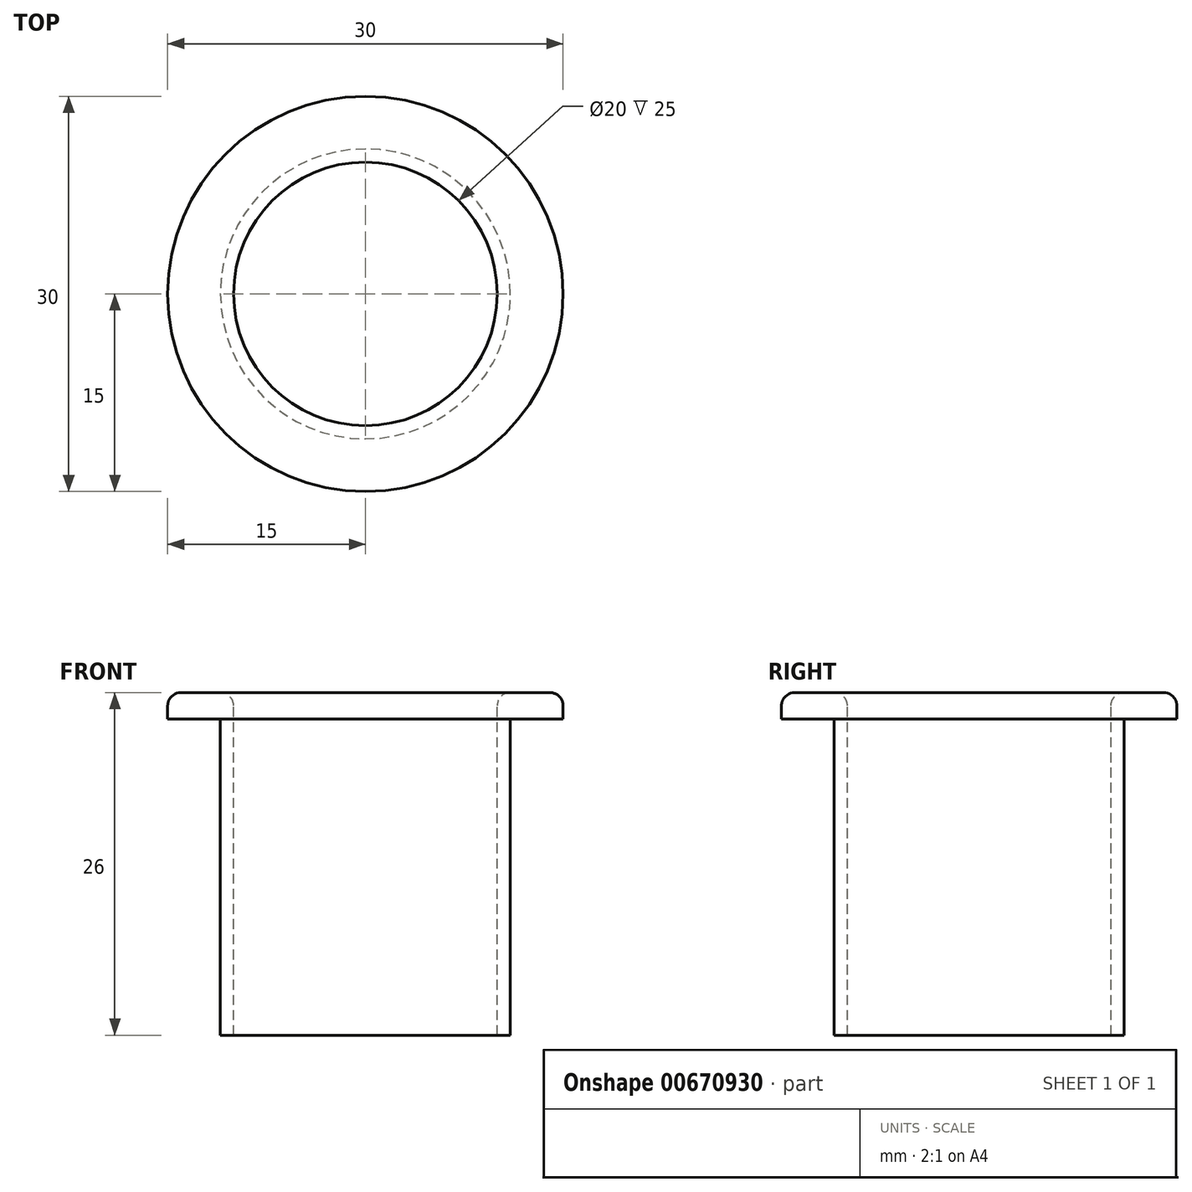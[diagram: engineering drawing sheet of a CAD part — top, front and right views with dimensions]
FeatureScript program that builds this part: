
annotation { "Feature Type Name" : "Feature", "Feature Type Description" : "" }
export const myFeature = defineFeature(function(context is Context, id is Id, definition is map)
    precondition{}
    {
        {
            var Q0;
            Q0=qCreatedBy(makeId("Top.planeOp"),FACE);
            var sketch = newSketch(context, id + "F0", { "sketchPlane" : qUnion([Q0])});
            skCircle(sketch, "E0", {"center": v(0, 0) * mm, "radius": 10 * mm});
            skCircle(sketch, "E1", {"center": v(0, 0) * mm, "radius": 15 * mm});
            skCircle(sketch, "E2", {"center": v(0, 0) * mm, "radius": 11 * mm});
            skSolve(sketch);
        }
        {
            var Q0;
            Q0=makeQuery(id+"F0.imprint","IMPRINT",FACE,{"disambiguationData":[TD([[makeQuery(id+"F0.imprint","IMPRINT",EDGE,{"derivedFrom":sQuery(id+"F0.wireOp",EDGE,"E0")}),-1.0]])]});
            extrude(context, id + "F1", {"entities" : qUnion([Q0]), "oppositeDirection" : true, "depth" : 24 * mm, "offsetDistance" : 25 * mm});
        }
        {
            var Q0;
            Q0=makeQuery(id+"F0.imprint","IMPRINT",FACE,{"disambiguationData":[TD([[makeQuery(id+"F0.imprint","IMPRINT",EDGE,{"derivedFrom":sQuery(id+"F0.wireOp",EDGE,"E0")}),-1.0]])]});
            var Q1;
            Q1=makeQuery(id+"F0.imprint","IMPRINT",FACE,{"disambiguationData":[TD([[makeQuery(id+"F0.imprint","IMPRINT",EDGE,{"derivedFrom":sQuery(id+"F0.wireOp",EDGE,"E1")}),1.0]])]});
            extrude(context, id + "F2", {"entities" : qUnion([Q0, Q1]), "operationType" : NewBodyOperationType.ADD, "depth" : 2 * mm, "offsetDistance" : 25 * mm});
        }
        {
            var Q0;
            Q0=makeQuery(id+"F2.opExtrude","CAP_EDGE",EDGE,{"disambiguationData":[OSD([sQuery(id+"F0.wireOp",EDGE,"E1")])],"isStart":false});
            var Q1;
            Q1=makeQuery(id+"F2.opExtrude","CAP_EDGE",EDGE,{"disambiguationData":[OSD([sQuery(id+"F0.wireOp",EDGE,"E0")])],"isStart":false});
            fillet(context, id + "F3", {"entities" : qUnion([Q0, Q1]), "radius" : 1 * mm, "tangentPropagation" : true, "allowEdgeOverflow" : false});
        }
    });
